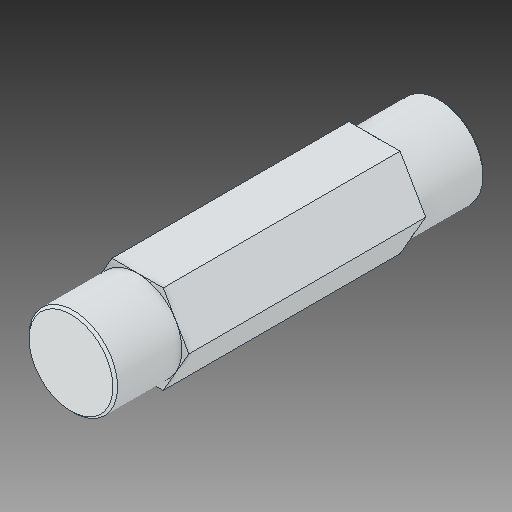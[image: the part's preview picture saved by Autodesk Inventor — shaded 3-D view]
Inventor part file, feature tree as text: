
AUTODESK INVENTOR PART (.ipt)
format: ipt  version: 2018 (Build 220112000, 112)  size: 102,400 bytes
history: native  units: in
note: dims shown in document units (in); Inventor stores cm internally (conversion verified against a paired STEP export)
features: chamfer x1
ambient origin geometry x8: Origin, YZ Plane, XZ Plane, XY Plane, X Axis, Y Axis, Z Axis, Center Point
bodies: Solid1 (feature_tree)
feature tree (1):
  chamfer  "Chamfer1"  [1 undecoded]
note: 1 required parameter value undecoded (feature->parameter linkage not recoverable at this tier; creation-order binding heuristic only, values carry confidence <= 0.55)
